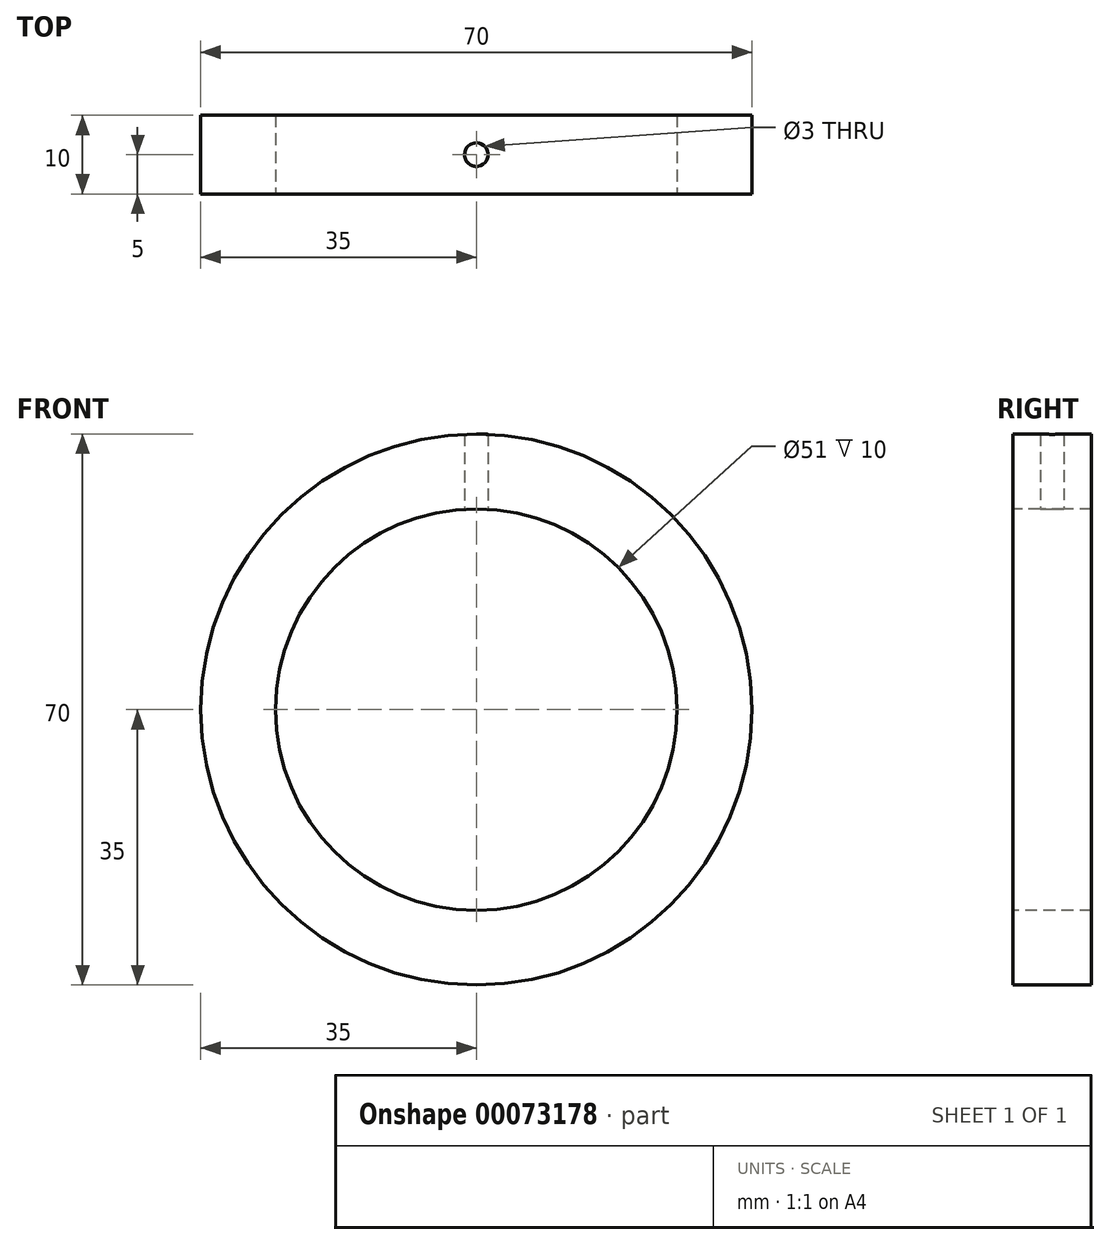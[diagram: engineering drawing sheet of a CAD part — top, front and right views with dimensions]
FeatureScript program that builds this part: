
annotation { "Feature Type Name" : "Feature", "Feature Type Description" : "" }
export const myFeature = defineFeature(function(context is Context, id is Id, definition is map)
    precondition{}
    {
        {
            var Q0;
            Q0=qCreatedBy(makeId("Front.planeOp"),FACE);
            var sketch = newSketch(context, id + "F0", { "sketchPlane" : qUnion([Q0])});
            skCircle(sketch, "E0", {"center": v(0, 0) * mm, "radius": 35 * mm});
            skSolve(sketch);
        }
        {
            var Q0;
            Q0 = qSketchRegion(id + "F0", true);
            extrude(context, id + "F1", {"entities" : qUnion([Q0]), "endBound" : BoundingType.SYMMETRIC, "depth" : 10 * mm});
        }
        {
            var Q0;
            Q0=makeQuery(id+"F0.imprint","IMPRINT",FACE,{"disambiguationData":[TD([[makeQuery(id+"F0.imprint","IMPRINT",EDGE,{"derivedFrom":sQuery(id+"F0.wireOp",EDGE,"E0")}),1.0]])]});
            var sketch = newSketch(context, id + "F2", { "sketchPlane" : qUnion([Q0])});
            skCircle(sketch, "E1", {"center": v(0, 0) * mm, "radius": 25.5 * mm});
            skSolve(sketch);
        }
        {
            var Q0;
            Q0 = qSketchRegion(id + "F2", true);
            extrude(context, id + "F3", {"entities" : qUnion([Q0]), "operationType" : NewBodyOperationType.REMOVE, "endBound" : BoundingType.SYMMETRIC, "oppositeDirection" : true, "depth" : 10 * mm});
        }
        {
            var Q0;
            Q0=qCreatedBy(makeId("Top.planeOp"),FACE);
            var sketch = newSketch(context, id + "F4", { "sketchPlane" : qUnion([Q0])});
            skCircle(sketch, "E2", {"center": v(0, 0) * mm, "radius": 1.5 * mm});
            skSolve(sketch);
        }
        {
            var Q0;
            Q0 = qSketchRegion(id + "F4", true);
            var Q1;
            Q1=sQuery(id+"F4.wireOp",EDGE,"E2");
            extrude(context, id + "F5", {"entities" : qUnion([Q0]), "operationType" : NewBodyOperationType.REMOVE, "surfaceEntities" : qUnion([Q1]), "depth" : 35 * mm});
        }
    });
